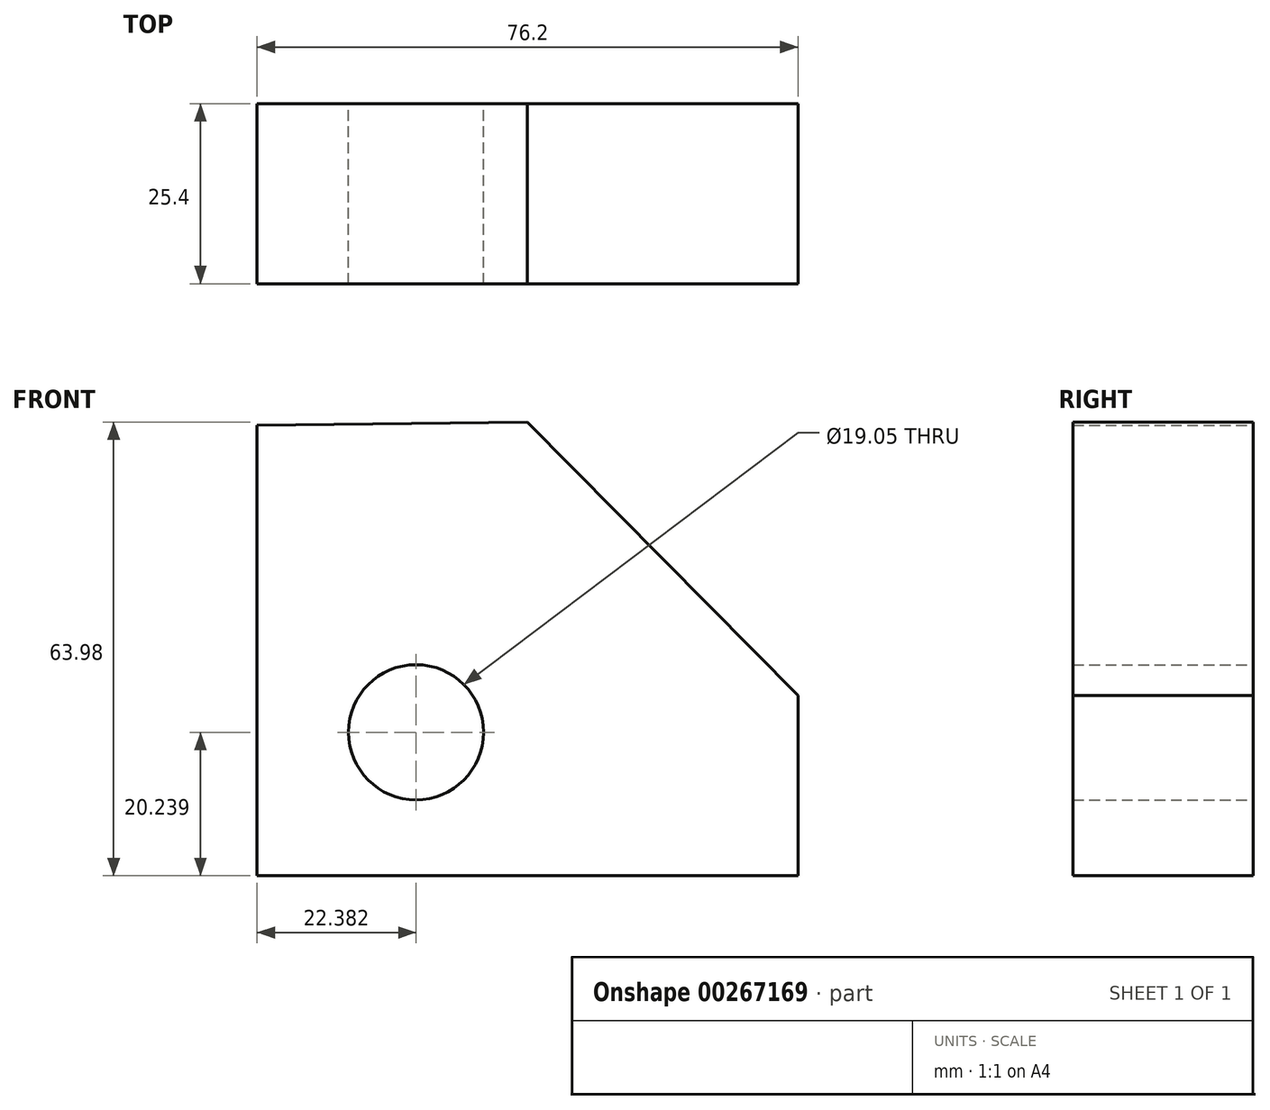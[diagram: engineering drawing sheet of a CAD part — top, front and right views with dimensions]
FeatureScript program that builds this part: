
annotation { "Feature Type Name" : "Feature", "Feature Type Description" : "" }
export const myFeature = defineFeature(function(context is Context, id is Id, definition is map)
    precondition{}
    {
        {
            var Q0;
            Q0=qCreatedBy(makeId("Front.planeOp"),FACE);
            var sketch = newSketch(context, id + "F0", { "sketchPlane" : qUnion([Q0])});
            skLineSegment(sketch, "E0", {"start": v(0, 63.5) * mm, "end": v(0, 0) * mm});
            skLineSegment(sketch, "E1", {"start": v(0, 0) * mm, "end": v(76.2, 0) * mm});
            skLineSegment(sketch, "E2", {"start": v(76.2, 0) * mm, "end": v(76.2, 25.4) * mm});
            skLineSegment(sketch, "E3", {"start": v(76.2, 25.4) * mm, "end": v(38.1, 63.98) * mm});
            skLineSegment(sketch, "E4", {"start": v(38.1, 63.98) * mm, "end": v(0, 63.5) * mm});
            skCircle(sketch, "E5", {"center": v(22.38, 20.24) * mm, "radius": 9.53 * mm});
            skSolve(sketch);
        }
        {
            var Q0;
            Q0=makeQuery(id+"F0.imprint","IMPRINT",FACE,{"disambiguationData":[TD([[makeQuery(id+"F0.imprint","IMPRINT",EDGE,{"derivedFrom":sQuery(id+"F0.wireOp",EDGE,"E0")}),1.0]])]});
            extrude(context, id + "F1", {"entities" : qUnion([Q0]), "depth" : 25.4 * mm, "symmetric" : true});
        }
    });
